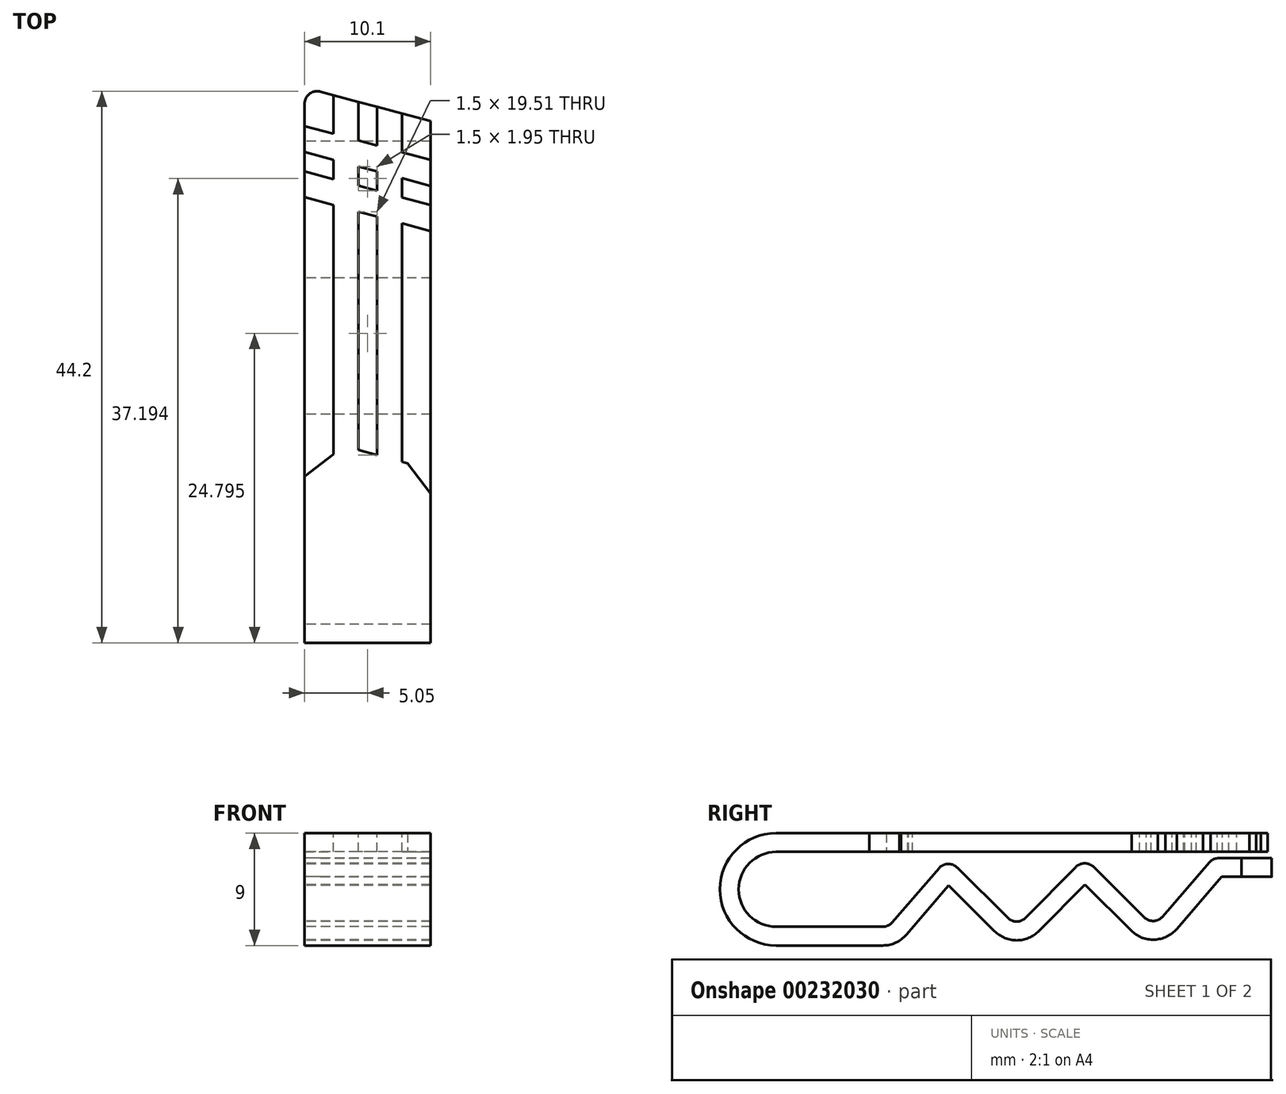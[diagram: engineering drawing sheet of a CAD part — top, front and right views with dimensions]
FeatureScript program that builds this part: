
annotation { "Feature Type Name" : "Feature", "Feature Type Description" : "" }
export const myFeature = defineFeature(function(context is Context, id is Id, definition is map)
    precondition{}
    {
        {
            var Q0;
            Q0=qCreatedBy(makeId("Right.planeOp"),FACE);
            var sketch = newSketch(context, id + "F0", { "sketchPlane" : qUnion([Q0])});
            skArc(sketch, "E0", {"start": v(0, 3) * mm, "mid": v(-3, 0) * mm, "end": v(0, -3) * mm});
            skLineSegment(sketch, "E1", {"start": v(0, -3) * mm, "end": v(8.54, -3) * mm});
            skLineSegment(sketch, "E2", {"start": v(0, 3) * mm, "end": v(40, 3) * mm});
            skLineSegment(sketch, "E3", {"start": v(9.3, -2.65) * mm, "end": v(13.04, 1.69) * mm});
            skLineSegment(sketch, "E4", {"start": v(14.5, 1.74) * mm, "end": v(18.57, -2.3) * mm});
            skLineSegment(sketch, "E5", {"start": v(19.99, -2.29) * mm, "end": v(24.01, 1.79) * mm});
            skLineSegment(sketch, "E6", {"start": v(25.43, 1.8) * mm, "end": v(29.5, -2.24) * mm});
            skLineSegment(sketch, "E7", {"start": v(30.96, -2.19) * mm, "end": v(34.7, 2.15) * mm});
            skLineSegment(sketch, "E8", {"start": v(35.46, 2.5) * mm, "end": v(40, 2.5) * mm});
            skPoint(sketch, "E9.visualSharp", {"position": v(9, -3) * mm});
            skArc(sketch, "E9.filletArc", {"start": v(8.54, -3) * mm, "mid": v(8.96, -2.9) * mm, "end": v(9.3, -2.65) * mm});
            skPoint(sketch, "E10.visualSharp", {"position": v(13.74, 2.5) * mm});
            skArc(sketch, "E10.filletArc", {"start": v(14.5, 1.74) * mm, "mid": v(13.76, 2.03) * mm, "end": v(13.04, 1.69) * mm});
            skPoint(sketch, "E11.visualSharp", {"position": v(19.28, -3) * mm});
            skArc(sketch, "E11.filletArc", {"start": v(18.57, -2.3) * mm, "mid": v(19.28, -2.58) * mm, "end": v(19.99, -2.29) * mm});
            skPoint(sketch, "E12.visualSharp", {"position": v(24.72, 2.5) * mm});
            skArc(sketch, "E12.filletArc", {"start": v(25.43, 1.8) * mm, "mid": v(24.72, 2.08) * mm, "end": v(24.01, 1.79) * mm});
            skPoint(sketch, "E13.visualSharp", {"position": v(30.26, -3) * mm});
            skArc(sketch, "E13.filletArc", {"start": v(29.5, -2.24) * mm, "mid": v(30.24, -2.53) * mm, "end": v(30.96, -2.19) * mm});
            skPoint(sketch, "E14.visualSharp", {"position": v(35, 2.5) * mm});
            skArc(sketch, "E14.filletArc", {"start": v(35.46, 2.5) * mm, "mid": v(35.04, 2.4) * mm, "end": v(34.7, 2.15) * mm});
            skLineSegment(sketch, "E15.0", {"start": v(35.69, 1) * mm, "end": v(40, 1) * mm});
            skLineSegment(sketch, "E15.1", {"start": v(32.1, -3.17) * mm, "end": v(35.69, 1) * mm});
            skArc(sketch, "E15.2", {"start": v(8.54, -4.5) * mm, "mid": v(9.58, -4.27) * mm, "end": v(10.44, -3.63) * mm});
            skLineSegment(sketch, "E15.3", {"start": v(0, -4.5) * mm, "end": v(8.54, -4.5) * mm});
            skArc(sketch, "E15.4", {"start": v(0, 4.5) * mm, "mid": v(-4.5, 0) * mm, "end": v(0, -4.5) * mm});
            skLineSegment(sketch, "E15.5", {"start": v(0, 4.5) * mm, "end": v(40, 4.5) * mm});
            skLineSegment(sketch, "E15.6", {"start": v(10.44, -3.63) * mm, "end": v(13.83, 0.3) * mm});
            skLineSegment(sketch, "E15.7", {"start": v(13.83, 0.3) * mm, "end": v(17.51, -3.36) * mm});
            skArc(sketch, "E15.8", {"start": v(17.51, -3.36) * mm, "mid": v(19.29, -4.08) * mm, "end": v(21.05, -3.34) * mm});
            skLineSegment(sketch, "E15.9", {"start": v(21.05, -3.34) * mm, "end": v(24.73, 0.38) * mm});
            skLineSegment(sketch, "E15.10", {"start": v(24.73, 0.38) * mm, "end": v(28.44, -3.3) * mm});
            skArc(sketch, "E15.11", {"start": v(28.44, -3.3) * mm, "mid": v(30.3, -4.03) * mm, "end": v(32.1, -3.17) * mm});
            skLineSegment(sketch, "E16", {"start": v(40, 4.5) * mm, "end": v(40, 3) * mm});
            skLineSegment(sketch, "E17", {"start": v(40, 1) * mm, "end": v(40, 2.5) * mm});
            skSolve(sketch);
        }
        {
            var Q0;
            Q0 = qSketchRegion(id + "F0", true);
            extrude(context, id + "F1", {"entities" : qUnion([Q0]), "depth" : 10.1 * mm});
        }
        {
            var Q0;
            Q0=makeQuery(id+"F1.opExtrude","SWEPT_FACE",FACE,{"disambiguationData":[OSD([sQuery(id+"F0.wireOp",EDGE,"E15.5")])]});
            var sketch = newSketch(context, id + "F2", { "sketchPlane" : qUnion([Q0])});
            skLineSegment(sketch, "E18", {"start": v(2.3, 39.38) * mm, "end": v(4.3, 38.85) * mm});
            skLineSegment(sketch, "E19", {"start": v(10.1, 37.3) * mm, "end": v(10.1, 40) * mm});
            skLineSegment(sketch, "E20", {"start": v(10.1, 40) * mm, "end": v(0, 40) * mm});
            skLineSegment(sketch, "E21.left", {"start": v(5.8, 38.45) * mm, "end": v(5.8, 35.34) * mm});
            skLineSegment(sketch, "E21.right", {"start": v(4.3, 38.85) * mm, "end": v(4.3, 35.74) * mm});
            skPoint(sketch, "E22.positionSnap0", {"position": v(5.05, 38.85) * mm});
            skPoint(sketch, "E23", {"position": v(5.05, 40) * mm});
            skPoint(sketch, "E24.orphan", {"position": v(5.8, 38.85) * mm});
            skLineSegment(sketch, "E25", {"start": v(4.3, 10.94) * mm, "end": v(5.8, 10.54) * mm});
            skLineSegment(sketch, "E26.trimOffspring", {"start": v(5.8, 38.45) * mm, "end": v(7.8, 37.9) * mm});
            skLineSegment(sketch, "E27", {"start": v(10.1, 9.39) * mm, "end": v(0, 12.1) * mm, "construction": true});
            skLineSegment(sketch, "E28", {"start": v(2.3, 11.48) * mm, "end": v(2.3, 30.58) * mm});
            skLineSegment(sketch, "E29", {"start": v(7.8, 10) * mm, "end": v(7.8, 29.11) * mm});
            skLineSegment(sketch, "E30", {"start": v(10.1, 28.5) * mm, "end": v(0, 31.2) * mm, "construction": true});
            skLineSegment(sketch, "E31", {"start": v(0, 33.27) * mm, "end": v(10.1, 30.56) * mm, "construction": true});
            skLineSegment(sketch, "E32", {"start": v(0, 36.9) * mm, "end": v(10.1, 34.19) * mm, "construction": true});
            skLineSegment(sketch, "E33", {"start": v(10.1, 32.12) * mm, "end": v(0, 34.82) * mm, "construction": true});
            skLineSegment(sketch, "E34", {"start": v(2.3, 11.48) * mm, "end": v(0, 12.1) * mm});
            skLineSegment(sketch, "E35", {"start": v(0, 31.2) * mm, "end": v(2.3, 30.58) * mm});
            skLineSegment(sketch, "E36", {"start": v(0, 33.27) * mm, "end": v(2.3, 32.65) * mm});
            skLineSegment(sketch, "E37", {"start": v(2.3, 32.65) * mm, "end": v(2.3, 34.2) * mm});
            skLineSegment(sketch, "E38", {"start": v(2.3, 34.2) * mm, "end": v(0, 34.82) * mm});
            skLineSegment(sketch, "E39", {"start": v(0, 33.27) * mm, "end": v(0, 34.82) * mm});
            skLineSegment(sketch, "E40", {"start": v(0, 36.9) * mm, "end": v(0, 40) * mm});
            skLineSegment(sketch, "E41", {"start": v(2.3, 39.38) * mm, "end": v(2.3, 36.28) * mm});
            skLineSegment(sketch, "E42", {"start": v(2.3, 36.28) * mm, "end": v(0, 36.9) * mm});
            skLineSegment(sketch, "E43", {"start": v(0, 12.1) * mm, "end": v(0, 31.2) * mm});
            skLineSegment(sketch, "E44.trimOffspring", {"start": v(2.3, 36.28) * mm, "end": v(2.3, 39.38) * mm});
            skLineSegment(sketch, "E45", {"start": v(7.8, 10) * mm, "end": v(10.1, 9.39) * mm});
            skLineSegment(sketch, "E46", {"start": v(10.1, 28.5) * mm, "end": v(7.8, 29.11) * mm});
            skLineSegment(sketch, "E47", {"start": v(7.8, 29.11) * mm, "end": v(7.8, 10) * mm});
            skLineSegment(sketch, "E48", {"start": v(7.8, 31.18) * mm, "end": v(7.8, 32.73) * mm});
            skLineSegment(sketch, "E49", {"start": v(7.8, 32.73) * mm, "end": v(10.1, 32.12) * mm});
            skLineSegment(sketch, "E50", {"start": v(10.1, 30.56) * mm, "end": v(7.8, 31.18) * mm});
            skLineSegment(sketch, "E51", {"start": v(10.1, 30.56) * mm, "end": v(10.1, 32.12) * mm});
            skLineSegment(sketch, "E52", {"start": v(10.1, 34.19) * mm, "end": v(7.8, 34.8) * mm});
            skLineSegment(sketch, "E53", {"start": v(7.8, 34.8) * mm, "end": v(7.8, 37.9) * mm});
            skLineSegment(sketch, "E54", {"start": v(10.1, 37.3) * mm, "end": v(10.1, 34.19) * mm});
            skLineSegment(sketch, "E55", {"start": v(4.3, 30.05) * mm, "end": v(5.8, 29.65) * mm});
            skLineSegment(sketch, "E56.trimOffspring", {"start": v(4.3, 30.05) * mm, "end": v(4.3, 10.94) * mm});
            skLineSegment(sketch, "E57.trimOffspring", {"start": v(5.8, 29.65) * mm, "end": v(5.8, 10.54) * mm});
            skLineSegment(sketch, "E58", {"start": v(5.8, 31.72) * mm, "end": v(4.3, 32.12) * mm});
            skLineSegment(sketch, "E59", {"start": v(5.8, 33.27) * mm, "end": v(4.3, 33.67) * mm});
            skLineSegment(sketch, "E60.trimOffspring", {"start": v(4.3, 33.67) * mm, "end": v(4.3, 32.12) * mm});
            skLineSegment(sketch, "E61.trimOffspring", {"start": v(5.8, 33.27) * mm, "end": v(5.8, 31.72) * mm});
            skLineSegment(sketch, "E62", {"start": v(5.8, 35.34) * mm, "end": v(4.3, 35.74) * mm});
            skLineSegment(sketch, "E63", {"start": v(10.1, 9.39) * mm, "end": v(10.1, 28.5) * mm});
            skSolve(sketch);
        }
        {
            var Q0;
            Q0 = qSketchRegion(id + "F2", true);
            extrude(context, id + "F3", {"entities" : qUnion([Q0]), "operationType" : NewBodyOperationType.REMOVE, "endBound" : BoundingType.UP_TO_NEXT, "oppositeDirection" : true, "depth" : 25 * mm});
        }
        {
            var Q0;
            Q0=makeQuery(id+"F1.opExtrude","SWEPT_FACE",FACE,{"disambiguationData":[OSD([sQuery(id+"F0.wireOp",EDGE,"E8")])]});
            var sketch = newSketch(context, id + "F4", { "sketchPlane" : qUnion([Q0])});
            skLineSegment(sketch, "E64", {"start": v(0, 40) * mm, "end": v(10.1, 37.3) * mm});
            skLineSegment(sketch, "E65", {"start": v(10.1, 37.3) * mm, "end": v(10.1, 40) * mm});
            skLineSegment(sketch, "E66", {"start": v(10.1, 40) * mm, "end": v(0, 40) * mm});
            skSolve(sketch);
        }
        {
            var Q0;
            Q0 = qSketchRegion(id + "F4", true);
            extrude(context, id + "F5", {"entities" : qUnion([Q0]), "operationType" : NewBodyOperationType.REMOVE, "oppositeDirection" : true, "depth" : 25 * mm});
        }
        {
            var Q0;
            Q0=makeQuery(id+"F3.boolean.opBoolean","COPY",EDGE,{"derivedFrom":makeQuery(id+"F3.opExtrude","SWEPT_EDGE",EDGE,{"disambiguationData":[OSD([sQuery(id+"F0.wireOp",EDGE,"E15.5"),sQuery(id+"F2.wireOp",EDGE,"E45"),sQuery(id+"F2.wireOp",EDGE,"E63")])]})});
            var Q1;
            Q1=makeQuery(id+"F3.boolean.opBoolean","COPY",EDGE,{"derivedFrom":makeQuery(id+"F3.opExtrude","SWEPT_EDGE",EDGE,{"disambiguationData":[OSD([sQuery(id+"F0.wireOp",EDGE,"E15.5"),sQuery(id+"F2.wireOp",EDGE,"E34"),sQuery(id+"F2.wireOp",EDGE,"E43")])]})});
            chamfer(context, id + "F6", {"entities" : qUnion([Q0, Q1]), "width" : 2.5 * mm, "tangentPropagation" : true});
        }
        {
            var Q0;
            Q0=makeQuery(id+"F5.boolean.opBoolean","MERGE",EDGE,{"derivedFrom":[makeQuery(id+"F1.opExtrude","CAP_EDGE",EDGE,{"disambiguationData":[OSD([sQuery(id+"F0.wireOp",EDGE,"E17")])],"isStart":true}),makeQuery(id+"F5.opExtrude","SWEPT_EDGE",EDGE,{"disambiguationData":[OSD([sQuery(id+"F0.wireOp",EDGE,"E8"),sQuery(id+"F4.wireOp",EDGE,"E64"),sQuery(id+"F4.wireOp",EDGE,"E66")])]})]});
            var Q1;
            Q1=makeQuery(id+"F5.boolean.opBoolean","COPY",EDGE,{"derivedFrom":makeQuery(id+"F5.opExtrude","SWEPT_EDGE",EDGE,{"disambiguationData":[OSD([sQuery(id+"F0.wireOp",EDGE,"E8"),sQuery(id+"F4.wireOp",EDGE,"E64"),sQuery(id+"F4.wireOp",EDGE,"E65")])]})});
            fillet(context, id + "F7", {"entities" : qUnion([Q0, Q1]), "radius" : 1 * mm, "tangentPropagation" : true, "allowEdgeOverflow" : false});
        }
    });
